# Revit family: Скамейка стальная «Флеш» без спинки Арт 12708
name_source: partatom
category: Антураж
revit_build: Autodesk Revit 2018 (Build: 20180423_1000(x64)
units: mm (PartAtom-declared; Revit-internal decimal feet)

## family parameters
Всегда вертикально = Да
Источник визуального образа = Геометрия семейства
На основе рабочей плоскости = Нет
Общий = Нет
При загрузке вырезать с полостями = Нет
Точка расчета площади = Нет

## types (4) — shared parameters
URL = https://hobbyka.ru
Артикул товара = Арт. 12708
Высота = 450 мм
Группа модели = Садовые скамейки
Изготовитель = ООО «Хоббика»
Изображение типоразмера = Скамейка стальная «Флеш» без спинки Арт 12708.jpg
Материал изделия = Сталь, дерево
Отступ = 1 мм
Цвет каркаса = Сталь
Цвет сидения = Дерево Тик
Ширина = 450 мм

## per-type parameters (varying)
| type | L1 | Длина | Модель 1,2 м | Модель 1,5 м | Модель 1,8 м | Модель 2,1 м | Описание |
| Модель 1,2 м | 900 мм | 1200 мм | Да | Нет | Нет | Нет | Скамейка стальная «Флеш» без спинки, модель 1,2 м |
| Модель 1,5 м | 1200 мм | 1500 мм | Нет | Да | Нет | Нет | Скамейка стальная «Флеш» без спинки, модель 1,5 м |
| Модель 1,8 м | 1500 мм | 1800 мм | Нет | Нет | Да | Нет | Скамейка стальная «Флеш» без спинки, модель 1,8 м |
| Модель 2,1 м | 1800 мм | 2100 мм | Нет | Нет | Нет | Да | Скамейка стальная «Флеш» без спинки, модель 2,1 м |
